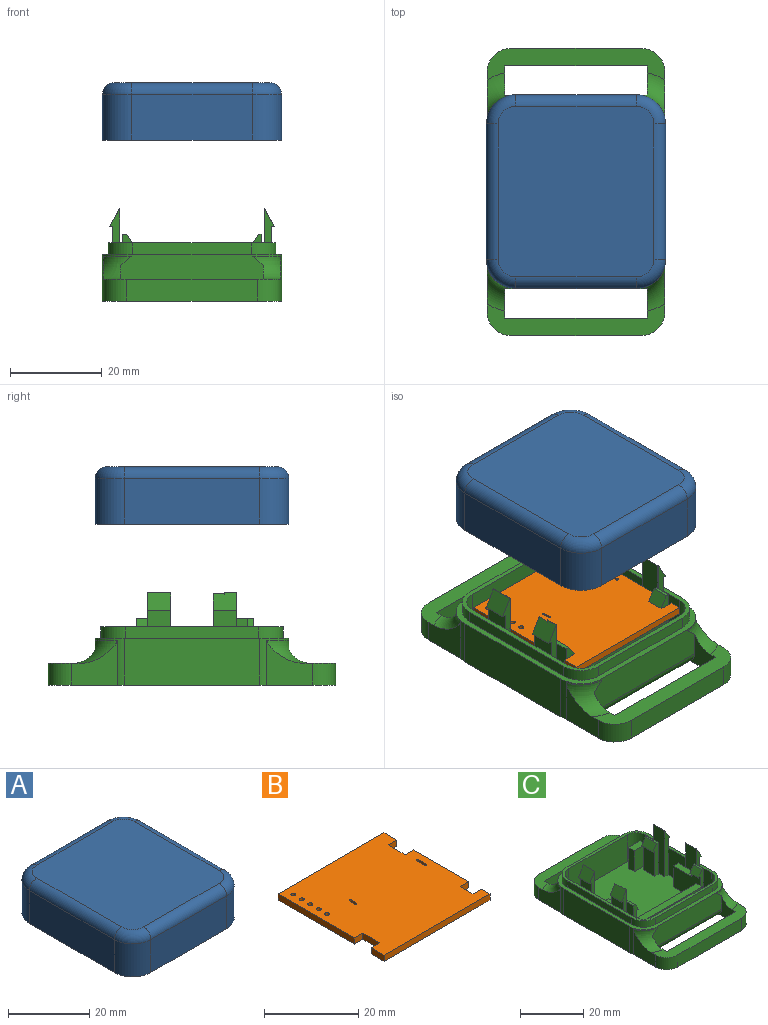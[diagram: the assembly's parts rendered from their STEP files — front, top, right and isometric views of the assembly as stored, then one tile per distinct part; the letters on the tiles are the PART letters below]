
ASSEMBLY  parts=3 mates=3
PART A: 52 faces, bbox 40x43.2x12.4 mm
  f0: plane 29.46x7.11mm, normal (-1,0,0), area 154.7mm2, adj f28,f29,f30,f31,f45,f46,f47,f48
  f1: plane 29.46x7.11mm, normal (1,0,0), area 154.7mm2, adj f28,f29,f33,f34,f36,f37,f38,f40
  f2: plane 42.16x38.99mm, normal (0,0,-1), area 150.6mm2, adj f3,f4,f5,f6,f7,f8,f9,f10
  f3: plane 26.29x9.91mm, normal (0,1,0), area 260.4mm2, adj f2,f4,f10,f15
  f4: cylinder r=6.35mm len=9.91mm, axis (0,0,-1), area 98.8mm2, adj f2,f3,f5,f13
  f5: plane 29.46x9.91mm, normal (-1,0,0), area 291.9mm2, adj f2,f4,f6,f12
  f6: cylinder r=6.35mm len=9.91mm, axis (0,0,-1), area 98.8mm2, adj f2,f5,f7,f14
  f7: plane 26.29x9.91mm, normal (0,-1,0), area 260.4mm2, adj f2,f6,f8,f16
  f8: cylinder r=6.35mm len=9.91mm, axis (0,0,-1), area 98.8mm2, adj f2,f7,f9,f18
  f9: plane 29.46x9.91mm, normal (1,0,0), area 291.9mm2, adj f2,f8,f10,f19
  f10: cylinder r=6.35mm len=9.91mm, axis (0,0,-1), area 98.8mm2, adj f2,f3,f9,f17
  f11: plane 37.08x33.91mm, normal (0,0,1), area 1245mm2, adj f12,f13,f14,f15,f16,f17,f18,f19
  f12: cylinder r=2.54mm len=29.46mm, axis (0,1,0), area 117.6mm2, adj f5,f11,f13,f14
  f13: torus R=3.81mm, axis (0,0,1), area 34mm2, adj f4,f11,f12,f15
  f14: torus R=3.81mm, axis (0,0,1), area 34mm2, adj f6,f11,f12,f16
  f15: cylinder r=2.54mm len=26.29mm, axis (1,0,0), area 104.9mm2, adj f3,f11,f13,f17
  f16: cylinder r=2.54mm len=26.29mm, axis (-1,0,0), area 104.9mm2, adj f7,f11,f14,f18
  f17: torus R=3.81mm, axis (0,0,1), area 34mm2, adj f10,f11,f15,f19
  f18: torus R=3.81mm, axis (0,0,1), area 34mm2, adj f8,f11,f16,f19
  f19: cylinder r=2.54mm len=29.46mm, axis (0,-1,0), area 117.6mm2, adj f9,f11,f17,f18
  f20: plane 29.46x3.05mm, normal (-1,0,0), area 89.8mm2, adj f2,f21,f27,f28
  f21: cylinder r=5.33mm len=5.33mm, axis (0,0,-1), area 25.5mm2, adj f2,f20,f22,f28
  f22: plane 26.29x3.05mm, normal (0,1,0), area 80.1mm2, adj f2,f21,f23,f28
  f23: cylinder r=5.33mm len=5.33mm, axis (0,0,-1), area 25.5mm2, adj f2,f22,f24,f28
  f24: plane 29.46x3.05mm, normal (1,0,0), area 89.8mm2, adj f2,f23,f25,f28
  f25: cylinder r=5.33mm len=5.33mm, axis (0,0,-1), area 25.5mm2, adj f2,f24,f26,f28
  f26: plane 26.29x3.05mm, normal (0,-1,0), area 80.1mm2, adj f2,f25,f27,f28
  f27: cylinder r=5.33mm len=5.33mm, axis (0,0,-1), area 25.5mm2, adj f2,f20,f26,f28
  f28: plane 40.13x36.96mm, normal (0,0,-1), area 179.1mm2, adj f0,f1,f20,f21,f22,f23,f24,f25
  f29: plane 37.59x36.45mm, normal (0,0,-1), area 1305.4mm2, adj f0,f1,f30,f31,f32,f33,f34,f35
  f30: cylinder r=4.06mm len=7.11mm, axis (0,0,-1), area 45.4mm2, adj f0,f28,f29,f35
  f31: cylinder r=4.06mm len=7.11mm, axis (0,0,-1), area 45.4mm2, adj f0,f28,f29,f32
  f32: plane 26.29x7.11mm, normal (0,1,0), area 187mm2, adj f28,f29,f31,f33
  f33: cylinder r=4.06mm len=7.11mm, axis (0,0,-1), area 45.4mm2, adj f1,f28,f29,f32
  f34: cylinder r=4.06mm len=7.11mm, axis (0,0,-1), area 45.4mm2, adj f1,f28,f29,f35
  f35: plane 26.29x7.11mm, normal (0,-1,0), area 187mm2, adj f28,f29,f30,f34
  f36: plane 4.32x1.02mm, normal (0,1,0), area 4.4mm2, adj f1,f29,f37,f39
  f37: plane 6.35x1.02mm, normal (0,0,1), area 6.5mm2, adj f1,f36,f38,f39
  f38: plane 4.32x1.02mm, normal (0,-1,0), area 4.4mm2, adj f1,f29,f37,f39
  f39: plane 6.35x4.32mm, normal (1,0,0), area 27.4mm2, adj f29,f36,f37,f38
  f40: plane 4.32x1.02mm, normal (0,1,0), area 4.4mm2, adj f1,f29,f41,f43
  f41: plane 6.35x1.02mm, normal (0,0,1), area 6.5mm2, adj f1,f40,f42,f43
  f42: plane 4.32x1.02mm, normal (0,-1,0), area 4.4mm2, adj f1,f29,f41,f43
  f43: plane 6.35x4.32mm, normal (1,0,0), area 27.4mm2, adj f29,f40,f41,f42
  f44: plane 6.35x4.32mm, normal (-1,0,0), area 27.4mm2, adj f29,f45,f46,f47
  f45: plane 6.35x1.02mm, normal (0,0,1), area 6.5mm2, adj f0,f44,f46,f47
  f46: plane 4.32x1.02mm, normal (0,-1,0), area 4.4mm2, adj f0,f29,f44,f45
  f47: plane 4.32x1.02mm, normal (0,1,0), area 4.4mm2, adj f0,f29,f44,f45
  f48: plane 4.32x1.02mm, normal (0,1,0), area 4.4mm2, adj f0,f29,f49,f51
  f49: plane 6.35x1.02mm, normal (0,0,1), area 6.5mm2, adj f0,f48,f50,f51
  f50: plane 4.32x1.02mm, normal (0,-1,0), area 4.4mm2, adj f0,f29,f49,f51
  f51: plane 6.35x4.32mm, normal (-1,0,0), area 27.4mm2, adj f29,f48,f49,f50
PART B: 31 faces, bbox 31.8x31.8x1.6 mm
  f0: plane 31.75x1.6mm, normal (0,-1,0), area 50.8mm2, adj f1,f2,f3,f4
  f1: plane 2.54x1.6mm, normal (1,0,0), area 4.1mm2, adj f0,f3,f4,f5
  f2: plane 3.81x1.6mm, normal (-1,0,0), area 6.1mm2, adj f0,f3,f4,f6
  f3: plane 31.75x31.75mm, normal (0,0,-1), area 966.2mm2, adj f0,f1,f2,f5,f6,f7,f8,f9
  f4: plane 31.75x31.75mm, normal (0,0,1), area 966.2mm2, adj f0,f1,f2,f5,f6,f7,f8,f9
  f5: plane 2.54x1.6mm, normal (0,1,0), area 4.1mm2, adj f1,f3,f4,f7
  f6: plane 2.54x1.6mm, normal (0,1,0), area 4.1mm2, adj f2,f3,f4,f8
  f7: plane 3.81x1.6mm, normal (1,0,0), area 6.1mm2, adj f3,f4,f5,f9
  f8: plane 5.08x1.6mm, normal (-1,0,0), area 8.1mm2, adj f3,f4,f6,f10
  f9: plane 2.54x1.6mm, normal (0,-1,0), area 4.1mm2, adj f3,f4,f7,f11
  f10: plane 2.54x1.6mm, normal (0,-1,0), area 4.1mm2, adj f3,f4,f8,f12
  f11: plane 16.51x1.6mm, normal (1,0,0), area 26.4mm2, adj f3,f4,f9,f13
  f12: plane 22.86x1.6mm, normal (-1,0,0), area 36.6mm2, adj f3,f4,f10,f14
  f13: plane 2.54x1.6mm, normal (0,1,0), area 4.1mm2, adj f3,f4,f11,f15
  f14: plane 31.75x1.6mm, normal (0,1,0), area 50.8mm2, adj f3,f4,f12,f16
  f15: plane 5.08x1.6mm, normal (1,0,0), area 8.1mm2, adj f3,f4,f13,f17
  f16: plane 3.81x1.6mm, normal (1,0,0), area 6.1mm2, adj f3,f4,f14,f17
  f17: plane 2.54x1.6mm, normal (0,-1,0), area 4.1mm2, adj f3,f4,f15,f16
  f18: plane 2.5x1.6mm, normal (-1,0,0), area 4mm2, adj f3,f4,f19,f20
  f19: cylinder r=0.25mm len=1.6mm, axis (0,0,-1), area 1.3mm2, adj f3,f4,f18,f21
  f20: cylinder r=0.25mm len=1.6mm, axis (0,0,-1), area 1.3mm2, adj f3,f4,f18,f21
  f21: plane 2.5x1.6mm, normal (1,0,0), area 4mm2, adj f3,f4,f19,f20
  f22: cylinder r=0.5mm len=1.6mm, axis (0,0,1), area 5mm2, adj f3,f4
  f23: cylinder r=0.5mm len=1.6mm, axis (0,0,1), area 5mm2, adj f3,f4
  f24: cylinder r=0.5mm len=1.6mm, axis (0,0,1), area 5mm2, adj f3,f4
  f25: cylinder r=0.5mm len=1.6mm, axis (0,0,1), area 5mm2, adj f3,f4
  f26: cylinder r=0.25mm len=1.6mm, axis (0,0,-1), area 1.3mm2, adj f3,f4,f27,f28
  f27: plane 1.6x1.6mm, normal (1,0,0), area 2.6mm2, adj f3,f4,f26,f29
  f28: plane 1.6x1.6mm, normal (-1,0,0), area 2.6mm2, adj f3,f4,f26,f29
  f29: cylinder r=0.25mm len=1.6mm, axis (0,0,-1), area 1.3mm2, adj f3,f4,f27,f28
  f30: cylinder r=0.5mm len=1.6mm, axis (0,0,1), area 5mm2, adj f3,f4
PART C: 127 faces, bbox 58x62.6x20.2 mm
  f0: plane 37.59x34.42mm, normal (0,0,1), area 1108.6mm2, adj f1,f2,f3,f4,f5,f6,f14,f15
  f1: plane 26.29x10.41mm, normal (0,-1,0), area 273.8mm2, adj f0,f2,f3,f11
  f2: cylinder r=4.06mm len=10.41mm, axis (0,0,-1), area 66.5mm2, adj f0,f1,f11,f19
  f3: cylinder r=4.06mm len=10.41mm, axis (0,0,-1), area 66.5mm2, adj f0,f1,f11,f14
  f4: plane 8.13x5.08mm, normal (0,1,0), area 41.3mm2, adj f0,f5,f6,f40
  f5: plane 8.13x2.54mm, normal (-1,0,0), area 20.6mm2, adj f0,f4,f39,f40
  f6: plane 8.13x2.54mm, normal (1,0,0), area 20.6mm2, adj f0,f4,f39,f40
  f7: cylinder r=6.35mm len=10.16mm, axis (0,0,-1), area 18.5mm2, adj f9,f10,f97,f98,f115,f121
  f8: cylinder r=6.35mm len=10.16mm, axis (0,0,-1), area 18.5mm2, adj f9,f10,f97,f102,f114,f122
  f9: plane 31.05x7.67mm, normal (0,1,0), area 229.7mm2, adj f7,f8,f97,f119,f120,f121,f122,f125
  f10: plane 62.48x38.99mm, normal (0,0,-1), area 1851.4mm2, adj f7,f8,f98,f99,f101,f102,f103,f105
  f11: plane 39.62x36.45mm, normal (0,0,1), area 140.2mm2, adj f1,f2,f3,f12,f13,f14,f15,f17
  f12: plane 5.08x3.56mm, normal (-1,0,0), area 18.1mm2, adj f11,f65,f66,f83
  f13: plane 5.08x3.56mm, normal (-1,0,0), area 18.1mm2, adj f11,f59,f60,f81
  f14: plane 10.41x5.08mm, normal (-1,0,0), area 52.9mm2, adj f0,f3,f11,f77
  f15: plane 10.41x9.14mm, normal (-1,0,0), area 95.2mm2, adj f0,f11,f72,f79
  f16: plane 8.13x3.3mm, normal (1,0,0), area 26.8mm2, adj f0,f28,f29,f72
  f17: plane 10.41x9.14mm, normal (1,0,0), area 95.2mm2, adj f0,f11,f60,f65
  f18: plane 8.13x0.57mm, normal (0,-1,0), area 4.6mm2, adj f0,f38,f46,f67
  f19: plane 10.41x5.08mm, normal (1,0,0), area 52.9mm2, adj f0,f2,f11,f59
  f20: plane 12.07x9.78mm, normal (-1,0,0), area 104.4mm2, adj f0,f28,f29,f41,f42,f57
  f21: plane 9.78x5.08mm, normal (-1,0,0), area 49.7mm2, adj f0,f49,f51,f55
  f22: plane 8.13x0.57mm, normal (0,-1,0), area 4.6mm2, adj f0,f29,f43,f73
  f23: plane 10.41x5.08mm, normal (1,0,0), area 52.9mm2, adj f0,f11,f24,f66
  f24: cylinder r=4.06mm len=10.41mm, axis (0,0,-1), area 66.5mm2, adj f0,f11,f23,f25
  f25: plane 26.29x10.41mm, normal (0,1,0), area 273.8mm2, adj f0,f11,f24,f26
  f26: cylinder r=4.06mm len=10.41mm, axis (0,0,-1), area 66.5mm2, adj f0,f11,f25,f27
  f27: plane 10.41x5.08mm, normal (-1,0,0), area 52.9mm2, adj f0,f11,f26,f74
  f28: plane 8.13x2.29mm, normal (0,1,0), area 18.6mm2, adj f0,f16,f20,f29
  f29: plane 8.26x2.29mm, normal (0,0,1), area 18.9mm2, adj f16,f20,f22,f28,f41,f69,f71
  f30: plane 27.95x8.13mm, normal (0,-1,0), area 227.2mm2, adj f0,f31,f33,f34
  f31: plane 8.13x2.54mm, normal (1,0,0), area 20.6mm2, adj f0,f30,f32,f34
  f32: plane 27.95x8.13mm, normal (0,1,0), area 227.2mm2, adj f0,f31,f33,f34
  f33: plane 8.13x2.54mm, normal (-1,0,0), area 20.6mm2, adj f0,f30,f32,f34
  f34: plane 27.95x2.54mm, normal (0,0,1), area 71mm2, adj f30,f31,f32,f33
  f35: plane 8.13x5.21mm, normal (-1,0,0), area 42.3mm2, adj f0,f37,f38,f65
  f36: plane 12.7x9.78mm, normal (1,0,0), area 111.6mm2, adj f0,f37,f38,f45,f47,f53
  f37: plane 8.13x2.29mm, normal (0,1,0), area 18.6mm2, adj f0,f35,f36,f38
  f38: plane 7.62x2.29mm, normal (0,0,1), area 17.4mm2, adj f18,f35,f36,f37,f45,f63,f64
  f39: plane 8.13x5.08mm, normal (0,-1,0), area 41.3mm2, adj f0,f5,f6,f40
  f40: plane 5.08x2.54mm, normal (0,0,1), area 12.9mm2, adj f4,f5,f6,f39
  f41: plane 4.19x2.29mm, normal (0,1,0), area 6.2mm2, adj f20,f29,f43,f44,f57,f58
  f42: plane 12.32x2.29mm, normal (0,-1,0), area 18.6mm2, adj f0,f20,f43,f44,f57,f58
  f43: plane 12.32x3.81mm, normal (1,0,0), area 46.9mm2, adj f0,f22,f41,f42,f44
  f44: plane 3.81x0.64mm, normal (0,0,1), area 2.4mm2, adj f41,f42,f43,f58
  f45: plane 4.19x2.54mm, normal (0,1,0), area 6.9mm2, adj f36,f38,f46,f48,f53,f54
  f46: plane 12.32x5.08mm, normal (-1,0,0), area 62.6mm2, adj f0,f18,f45,f47,f48
  f47: plane 12.32x2.54mm, normal (0,-1,0), area 19.3mm2, adj f0,f36,f46,f48,f53,f54
  f48: plane 5.08x0.89mm, normal (0,0,1), area 4.5mm2, adj f45,f46,f47,f54
  f49: plane 12.32x2.29mm, normal (0,-1,0), area 18.6mm2, adj f0,f21,f50,f52,f55,f56
  f50: plane 12.32x5.08mm, normal (1,0,0), area 62.6mm2, adj f0,f49,f51,f52
  f51: plane 12.32x2.29mm, normal (0,1,0), area 18.6mm2, adj f0,f21,f50,f52,f55,f56
  f52: plane 5.08x0.64mm, normal (0,0,1), area 3.2mm2, adj f49,f50,f51,f56
  f53: plane 5.08x1.02mm, normal (0,0,-1), area 5.2mm2, adj f36,f45,f47,f54
  f54: plane 5.08x2.54mm, normal (0.84,0,0.54), area 15.4mm2, adj f45,f47,f48,f53
  f55: plane 5.08x0.76mm, normal (0,0,-1), area 3.9mm2, adj f21,f49,f51,f56
  f56: plane 5.08x2.54mm, normal (-0.84,0,0.54), area 15.4mm2, adj f49,f51,f52,f55
  f57: plane 3.81x0.76mm, normal (0,0,-1), area 2.9mm2, adj f20,f41,f42,f58
  f58: plane 3.81x2.54mm, normal (-0.84,0,0.54), area 11.5mm2, adj f41,f42,f44,f57
  f59: plane 17.78x2.29mm, normal (0,1,0), area 25.8mm2, adj f0,f13,f19,f61,f62,f81,f82
  f60: plane 17.78x2.29mm, normal (0,-1,0), area 25.8mm2, adj f0,f13,f17,f61,f62,f81,f82
  f61: plane 17.78x5.08mm, normal (1,0,0), area 90.3mm2, adj f0,f59,f60,f62
  f62: plane 5.08x0.09mm, normal (0,0,1), area 0.4mm2, adj f59,f60,f61,f82
  f63: plane 9.47x2.41mm, normal (1,0,0), area 22.9mm2, adj f38,f64,f65,f84
  f64: plane 9.65x0.19mm, normal (0,1,0), area 1.8mm2, adj f38,f63,f67,f68,f84
  f65: plane 17.6x2.1mm, normal (0,1,0), area 22.4mm2, adj f0,f12,f17,f35,f63,f83,f84
  f66: plane 17.78x2.29mm, normal (0,-1,0), area 25.8mm2, adj f0,f12,f23,f67,f68,f83,f84
  f67: plane 17.78x2.67mm, normal (1,0,0), area 47.4mm2, adj f0,f18,f64,f66,f68
  f68: plane 2.67x0.09mm, normal (0,0,1), area 0.2mm2, adj f64,f66,f67,f84
  f69: plane 9.65x0.19mm, normal (0,1,0), area 1.8mm2, adj f29,f71,f73,f75,f86
  f70: plane 5.08x3.56mm, normal (1,0,0), area 18.1mm2, adj f11,f72,f74,f85
  f71: plane 9.47x4.95mm, normal (-1,0,0), area 46.9mm2, adj f29,f69,f72,f86
  f72: plane 17.6x2.1mm, normal (0,1,0), area 22.4mm2, adj f0,f15,f16,f70,f71,f85,f86
  f73: plane 17.78x0.13mm, normal (-1,0,0), area 2.3mm2, adj f0,f22,f69,f74,f75
  f74: plane 17.78x2.29mm, normal (0,-1,0), area 25.8mm2, adj f0,f27,f70,f73,f75,f85,f86
  f75: plane 0.13x0.09mm, normal (0,0,1), area 0mm2, adj f69,f73,f74,f86
  f76: plane 5.08x3.56mm, normal (1,0,0), area 18.1mm2, adj f11,f77,f79,f87
  f77: plane 17.78x2.29mm, normal (0,1,0), area 25.8mm2, adj f0,f14,f76,f78,f80,f87,f88
  f78: plane 17.78x5.08mm, normal (-1,0,0), area 90.3mm2, adj f0,f77,f79,f80
  f79: plane 17.78x2.29mm, normal (0,-1,0), area 25.8mm2, adj f0,f15,f76,f78,f80,f87,f88
  f80: plane 5.08x0.09mm, normal (0,0,1), area 0.4mm2, adj f77,f78,f79,f88
  f81: plane 5.08x0.76mm, normal (0,0,-1), area 3.9mm2, adj f13,f59,f60,f82
  f82: plane 5.08x3.81mm, normal (-0.87,0,0.5), area 22.3mm2, adj f59,f60,f62,f81
  f83: plane 5.08x0.76mm, normal (0,0,-1), area 3.9mm2, adj f12,f65,f66,f84
  f84: plane 5.08x3.81mm, normal (-0.87,0,0.5), area 21.8mm2, adj f63,f64,f65,f66,f68,f83
  f85: plane 5.08x0.76mm, normal (0,0,-1), area 3.9mm2, adj f70,f72,f74,f86
  f86: plane 5.08x3.81mm, normal (0.87,0,0.5), area 21.3mm2, adj f69,f71,f72,f74,f75,f85
  f87: plane 5.08x0.76mm, normal (0,0,-1), area 3.9mm2, adj f76,f77,f79,f88
  f88: plane 5.08x3.81mm, normal (0.87,0,0.5), area 22.3mm2, adj f77,f79,f80,f87
  f89: cylinder r=5.33mm len=5.33mm, axis (0,0,1), area 21.3mm2, adj f11,f90,f96,f97
  f90: plane 28.96x2.54mm, normal (1,0,0), area 73.5mm2, adj f11,f89,f91,f97
  f91: cylinder r=5.33mm len=5.33mm, axis (0,0,1), area 21.3mm2, adj f11,f90,f92,f97
  f92: plane 25.78x2.54mm, normal (0,-1,0), area 65.5mm2, adj f11,f91,f93,f97
  f93: cylinder r=5.33mm len=5.33mm, axis (0,0,1), area 21.3mm2, adj f11,f92,f94,f97
  f94: plane 28.96x2.54mm, normal (-1,0,0), area 73.5mm2, adj f11,f93,f95,f97
  f95: cylinder r=5.33mm len=5.33mm, axis (0,0,1), area 21.3mm2, adj f11,f94,f96,f97
  f96: plane 25.78x2.54mm, normal (0,1,0), area 65.5mm2, adj f11,f89,f95,f97
  f97: plane 42.16x38.99mm, normal (0,0,1), area 189.5mm2, adj f7,f8,f9,f89,f90,f91,f92,f93
  f98: plane 29.46x10.16mm, normal (1,0,0), area 299.4mm2, adj f7,f10,f97,f99
  f99: cylinder r=6.35mm len=10.16mm, axis (0,0,-1), area 18.5mm2, adj f10,f97,f98,f100,f106,f123
  f100: plane 31.05x7.67mm, normal (0,-1,0), area 229.7mm2, adj f97,f99,f101,f109,f110,f123,f124,f126
  f101: cylinder r=6.35mm len=10.16mm, axis (0,0,-1), area 18.5mm2, adj f10,f97,f100,f102,f105,f124
  f102: plane 29.46x10.16mm, normal (-1,0,0), area 299.4mm2, adj f8,f10,f97,f101
  f103: plane 28.46x4.74mm, normal (0,-1,0), area 134.8mm2, adj f10,f104,f107,f108
  f104: plane 38.62x6.88mm, normal (0,0,1), area 152.5mm2, adj f103,f105,f106,f107,f108,f109,f110,f111
  f105: plane 9.91x9.82mm, normal (-1,0,0), area 58.7mm2, adj f10,f101,f104,f107,f124
  f106: plane 9.91x9.82mm, normal (1,0,0), area 58.7mm2, adj f10,f99,f104,f108,f123
  f107: cylinder r=5.08mm len=5.08mm, axis (0,0,1), area 37.8mm2, adj f10,f103,f104,f105
  f108: cylinder r=5.08mm len=5.08mm, axis (0,0,-1), area 37.8mm2, adj f10,f103,f104,f106
  f109: plane 9.02x7.92mm, normal (-1,0,0), area 35.6mm2, adj f10,f100,f104,f111,f123,f126
  f110: plane 9.02x7.91mm, normal (1,0,0), area 35.6mm2, adj f10,f100,f104,f111,f124,f126
  f111: plane 31x4.74mm, normal (0,1,0), area 146.8mm2, adj f10,f104,f109,f110
  f112: plane 28.46x4.74mm, normal (0,1,0), area 134.8mm2, adj f10,f113,f116,f117
  f113: plane 38.62x6.88mm, normal (0,0,1), area 152.5mm2, adj f112,f114,f115,f116,f117,f118,f119,f120
  f114: plane 9.91x9.82mm, normal (-1,0,0), area 58.7mm2, adj f8,f10,f113,f116,f122
  f115: plane 9.91x9.82mm, normal (1,0,0), area 58.7mm2, adj f7,f10,f113,f117,f121
  f116: cylinder r=5.08mm len=5.08mm, axis (0,0,-1), area 37.8mm2, adj f10,f112,f113,f114
  f117: cylinder r=5.08mm len=5.08mm, axis (0,0,1), area 37.8mm2, adj f10,f112,f113,f115
  f118: plane 31x4.74mm, normal (0,-1,0), area 146.8mm2, adj f10,f113,f119,f120
  f119: plane 9.02x7.91mm, normal (-1,0,0), area 35.6mm2, adj f9,f10,f113,f118,f121,f125
  f120: plane 9.02x7.92mm, normal (1,0,0), area 35.6mm2, adj f9,f10,f113,f118,f122,f125
  f121: torus R=11.43mm, axis (0,0,-1), area 41.3mm2, adj f7,f9,f113,f115,f119
  f122: torus R=11.43mm, axis (0,0,-1), area 41.3mm2, adj f8,f9,f113,f114,f120
  f123: torus R=11.43mm, axis (0,0,1), area 41.3mm2, adj f99,f100,f104,f106,f109
  f124: torus R=11.43mm, axis (0,0,1), area 41.3mm2, adj f100,f101,f104,f105,f110
  f125: cylinder r=2.54mm len=31mm, axis (-1,0,0), area 123.7mm2, adj f9,f10,f119,f120
  f126: cylinder r=2.54mm len=31mm, axis (1,0,0), area 123.7mm2, adj f10,f100,f109,f110
PLACE A rot(axis=(0.01,-1,0.02),0deg) t=(10.76,19.26,28.02)mm
PLACE B t=(-111.06,100.47,3.39)mm
PLACE C rot(axis=(0.01,-1,0.02),0deg) t=(10.76,19.26,-7.02)mm
MATE slider A.f11 <-> C.f10  axis (0,0,1) through (10.76,19.26,40.47)mm
MATE planar B.f3 <-> C.f29  axis (0,0,-1) through (10.76,19.26,3.39)mm
MATE slider B.f4 <-> C.f10  axis (0,0,1) through (10.76,19.26,4.99)mm
